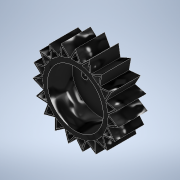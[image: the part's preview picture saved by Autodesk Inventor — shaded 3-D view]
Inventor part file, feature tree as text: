
AUTODESK INVENTOR PART (.ipt)
format: ipt  version: 2021 (Build 250183000, 183)  size: 215,040 bytes
history: native  units: mm
features: extrude x3, sketch x1, pattern_circular x1
ambient origin geometry x8: Origin, YZ Plane, XZ Plane, XY Plane, X Axis, Y Axis, Z Axis, Center Point
bodies: Solid1 (feature_tree)
feature tree (5):
  sketch  "Sketch1"  dims[d0=18.1mm d1=1.5mm d5=1.5mm d6=0.0mm d7=9.5mm d8=0.0mm d9=9.5mm d10=0.0mm d11=190.0mm d12=360.0deg d17=10.55mm d18=14.0mm d19=0.4mm d20=0.4mm d21=4.0mm d22=10.0mm d23=5.0mm d24=2.2mm d25=2.5mm]
  extrude  "Extrusion1"  Depth=1.5mm
  extrude  "Extrusion2"  Depth=1.5mm TaperAngle=0.0deg
  extrude  "Extrusion3"  Depth=9.5mm TaperAngle=0.0deg
  pattern_circular  "Circular Pattern1"  [2 undecoded]
note: 2 required parameter values undecoded (feature->parameter linkage not recoverable at this tier; creation-order binding heuristic only, values carry confidence <= 0.55)
